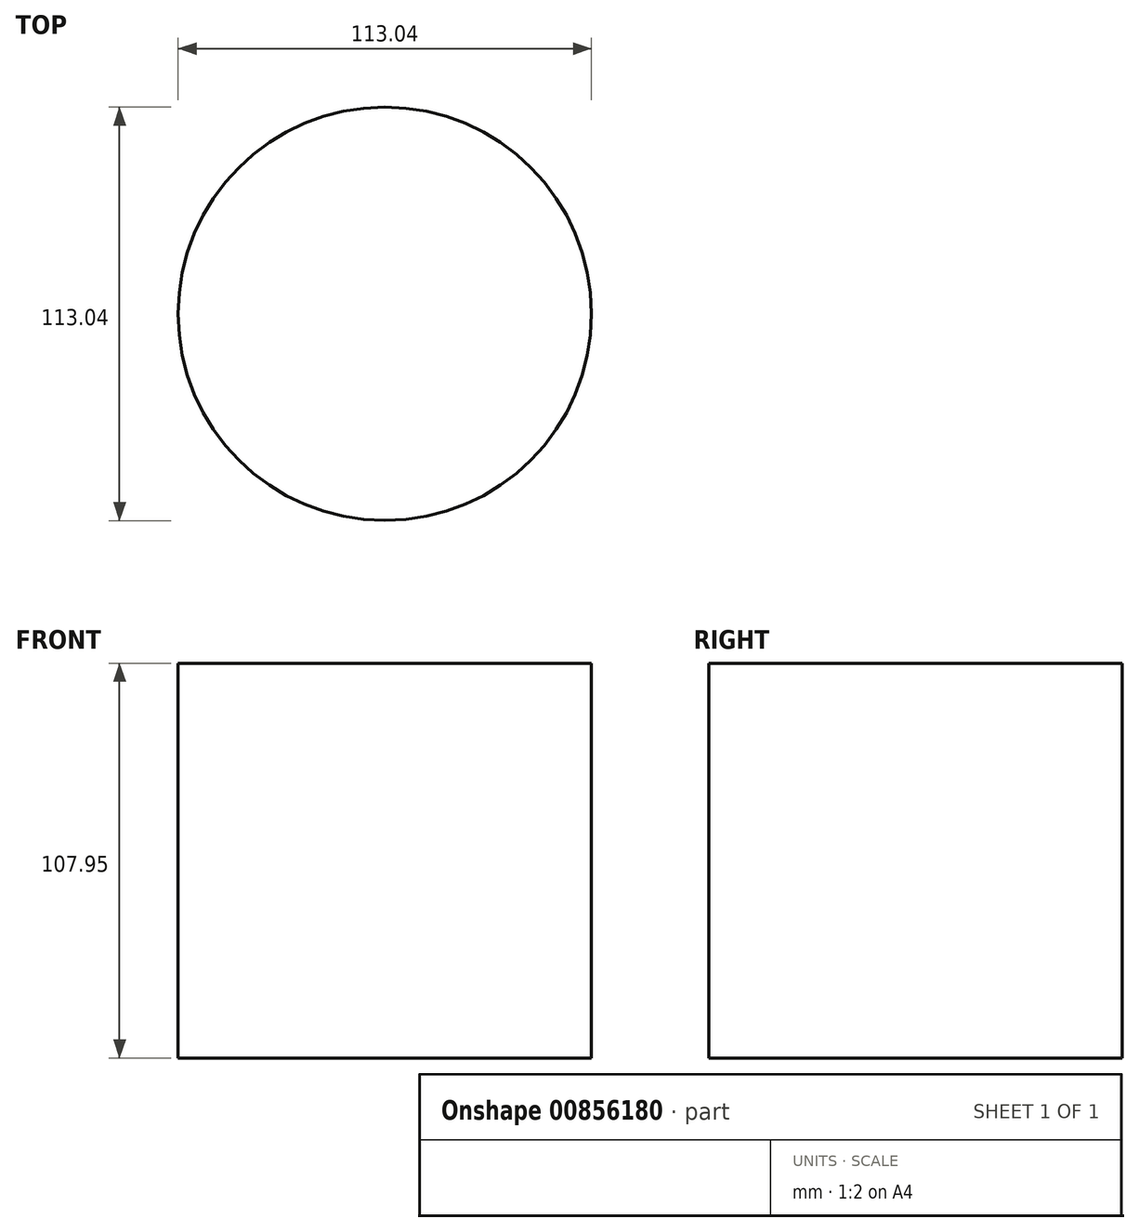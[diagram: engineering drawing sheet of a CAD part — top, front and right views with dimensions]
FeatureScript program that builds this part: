
annotation { "Feature Type Name" : "Feature", "Feature Type Description" : "" }
export const myFeature = defineFeature(function(context is Context, id is Id, definition is map)
    precondition{}
    {
        {
            var Q0;
            Q0=qCreatedBy(makeId("Top.planeOp"),FACE);
            var sketch = newSketch(context, id + "F0", { "sketchPlane" : qUnion([Q0])});
            skCircle(sketch, "E0", {"center": v(0, 0) * mm, "radius": 56.52 * mm});
            skCircle(sketch, "E1", {"center": v(0, 0) * mm, "radius": 51.44 * mm});
            skSolve(sketch);
        }
        {
            var Q0;
            Q0 = qSketchRegion(id + "F0", true);
            var Q1;
            Q1=makeQuery(id+"F0.imprint","IMPRINT",FACE,{"disambiguationData":[TD([[makeQuery(id+"F0.imprint","IMPRINT",EDGE,{"derivedFrom":sQuery(id+"F0.wireOp",EDGE,"E1")}),1.0]])]});
            extrude(context, id + "F1", {"entities" : qUnion([Q0, Q1]), "depth" : 107.95 * mm, "offsetDistance" : 25.4 * mm});
        }
    });
